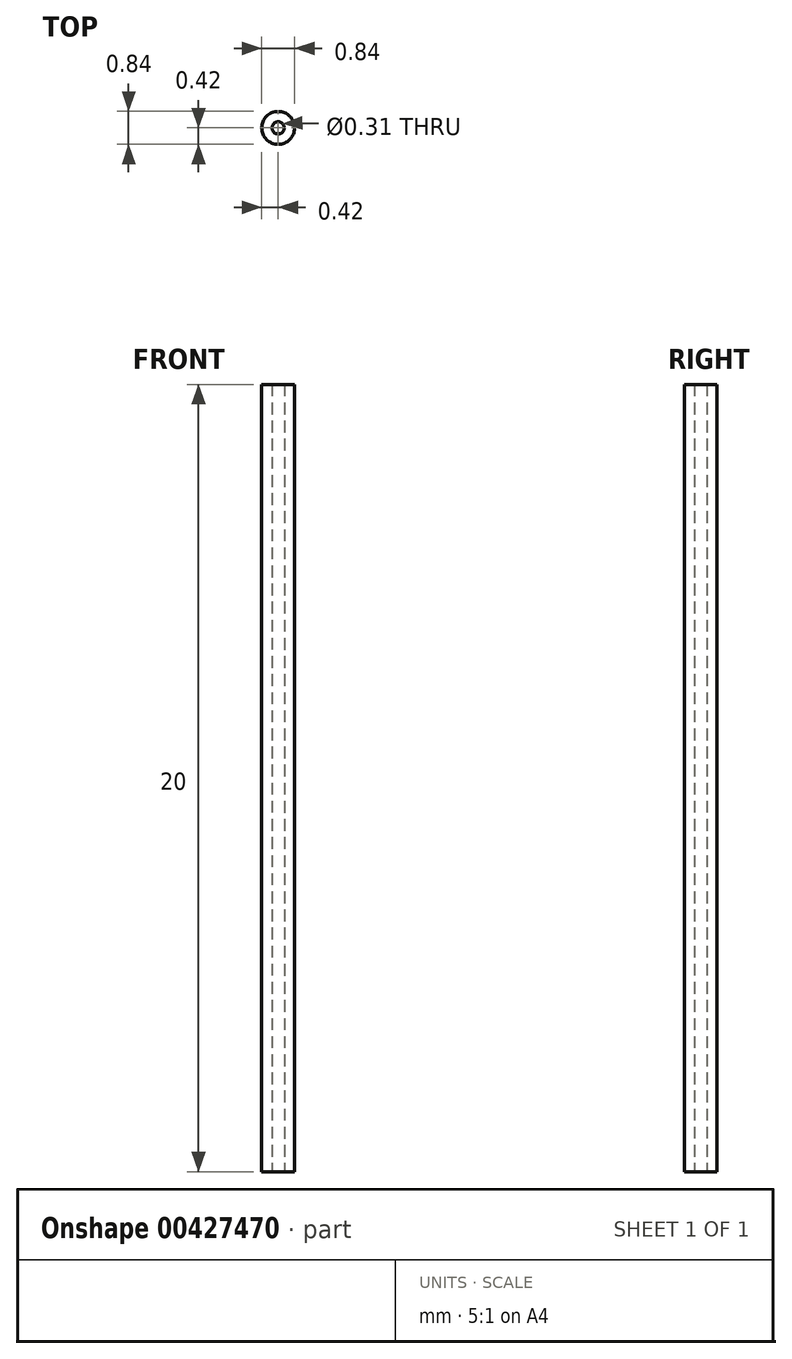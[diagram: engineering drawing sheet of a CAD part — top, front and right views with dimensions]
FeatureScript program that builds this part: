
annotation { "Feature Type Name" : "Feature", "Feature Type Description" : "" }
export const myFeature = defineFeature(function(context is Context, id is Id, definition is map)
    precondition{}
    {
        {
            var Q0;
            Q0=qCreatedBy(makeId("Top.planeOp"),FACE);
            var sketch = newSketch(context, id + "F0", { "sketchPlane" : qUnion([Q0])});
            skCircle(sketch, "E0", {"center": v(0, 0) * mm, "radius": 0.42 * mm});
            skCircle(sketch, "E1", {"center": v(0, 0) * mm, "radius": 0.16 * mm});
            skSolve(sketch);
        }
        {
            var Q0;
            Q0=makeQuery(id+"F0.imprint","IMPRINT",FACE,{"disambiguationData":[TD([[makeQuery(id+"F0.imprint","IMPRINT",EDGE,{"derivedFrom":sQuery(id+"F0.wireOp",EDGE,"E0")}),1.0]])]});
            extrude(context, id + "F1", {"entities" : qUnion([Q0]), "depth" : 20 * mm});
        }
    });
